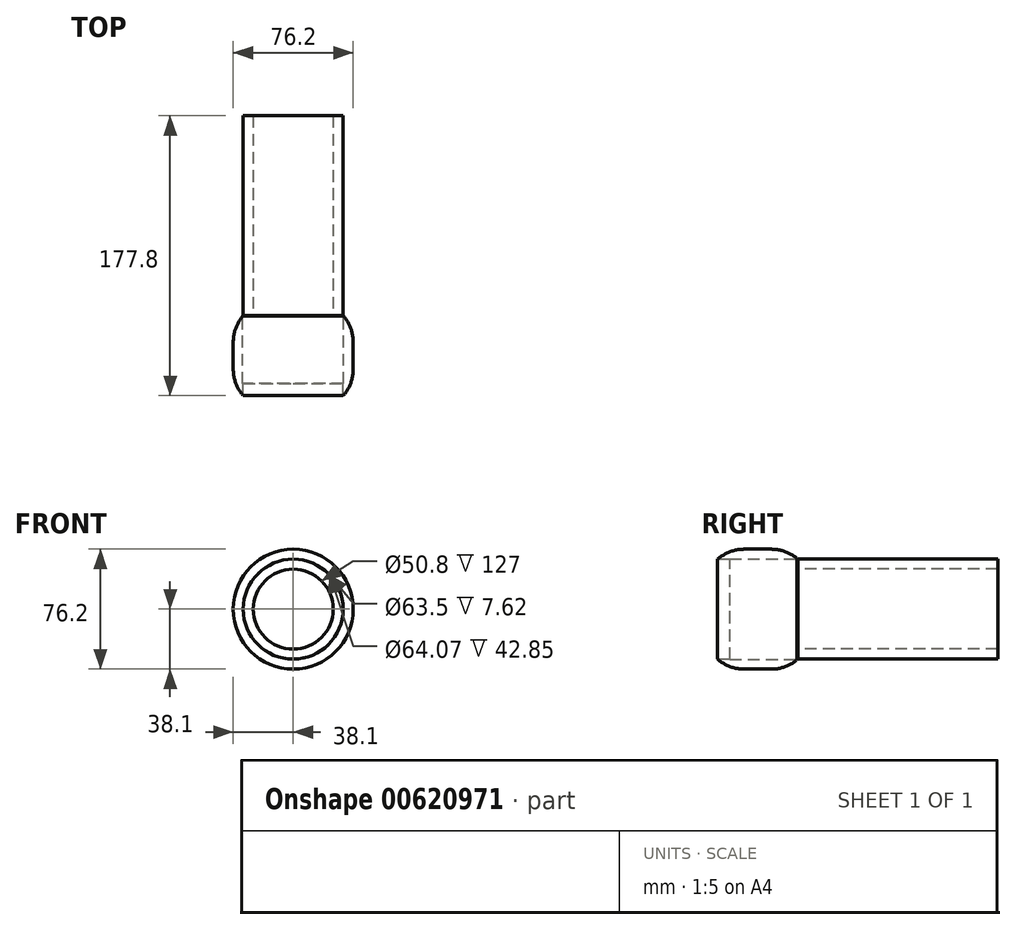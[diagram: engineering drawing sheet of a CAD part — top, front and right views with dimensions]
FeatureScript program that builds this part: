
annotation { "Feature Type Name" : "Feature", "Feature Type Description" : "" }
export const myFeature = defineFeature(function(context is Context, id is Id, definition is map)
    precondition{}
    {
        {
            var Q0;
            Q0=qCreatedBy(makeId("Front.planeOp"),FACE);
            var sketch = newSketch(context, id + "F0", { "sketchPlane" : qUnion([Q0])});
            skCircle(sketch, "E0", {"center": v(0, 0) * mm, "radius": 38.1 * mm});
            skCircle(sketch, "E1", {"center": v(0, 0) * mm, "radius": 31.75 * mm});
            skSolve(sketch);
        }
        {
            var Q0;
            Q0 = qSketchRegion(id + "F0", true);
            extrude(context, id + "F1", {"entities" : qUnion([Q0]), "depth" : 50.8 * mm, "offsetDistance" : 25.4 * mm});
        }
        {
            var Q0;
            Q0=makeQuery(id+"F1.opExtrude","CAP_EDGE",EDGE,{"disambiguationData":[OSD([sQuery(id+"F0.wireOp",EDGE,"E0")])],"isStart":false});
            fillet(context, id + "F2", {"entities" : qUnion([Q0]), "radius" : 25.4 * mm, "tangentPropagation" : true, "allowEdgeOverflow" : false});
        }
        {
            var Q0;
            Q0=makeQuery(id+"F1.opExtrude","CAP_EDGE",EDGE,{"disambiguationData":[OSD([sQuery(id+"F0.wireOp",EDGE,"E0")])],"isStart":true});
            fillet(context, id + "F3", {"entities" : qUnion([Q0]), "radius" : 25.4 * mm, "tangentPropagation" : true, "allowEdgeOverflow" : false});
        }
        {
            var Q0;
            Q0=qCreatedBy(makeId("Front.planeOp"),FACE);
            var sketch = newSketch(context, id + "F4", { "sketchPlane" : qUnion([Q0])});
            skCircle(sketch, "E2", {"center": v(0, 0) * mm, "radius": 32.04 * mm});
            skSolve(sketch);
        }
        {
            var Q0;
            Q0=makeQuery(id+"F4.imprint","IMPRINT",FACE,{"disambiguationData":[TD([[makeQuery(id+"F4.imprint","IMPRINT",EDGE,{"derivedFrom":sQuery(id+"F4.wireOp",EDGE,"E2")}),1.0]])]});
            extrude(context, id + "F5", {"entities" : qUnion([Q0]), "operationType" : NewBodyOperationType.REMOVE, "depth" : 43.18 * mm, "offsetDistance" : 25.4 * mm});
        }
        {
            var Q0;
            Q0=qCreatedBy(makeId("Front.planeOp"),FACE);
            var sketch = newSketch(context, id + "F6", { "sketchPlane" : qUnion([Q0])});
            skCircle(sketch, "E3", {"center": v(0, 0) * mm, "radius": 31.75 * mm});
            skCircle(sketch, "E4", {"center": v(0, 0) * mm, "radius": 25.4 * mm});
            skSolve(sketch);
        }
        {
            var Q0;
            Q0 = qSketchRegion(id + "F6", true);
            extrude(context, id + "F7", {"entities" : qUnion([Q0]), "operationType" : NewBodyOperationType.ADD, "oppositeDirection" : true, "depth" : 127 * mm, "offsetDistance" : 25.4 * mm});
        }
    });
